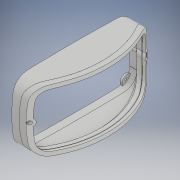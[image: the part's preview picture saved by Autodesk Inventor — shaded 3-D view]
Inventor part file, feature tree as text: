
AUTODESK INVENTOR PART (.ipt)
format: ipt  version: 2019 (Build 230136000, 136)  size: 3,016,704 bytes
history: native  units: mm
features: extrude x15, sketch x11, projected_geometry x7, other x4, hole x3, plane x3, fillet x1
ambient origin geometry x8: Origin, YZ Plane, XZ Plane, XY Plane, X Axis, Y Axis, Z Axis, Center Point
bodies: Volumenkörper3 (feature_tree), Volumenkörper7 (feature_tree), Volumenkörper8 (feature_tree), Volumenkörper9 (feature_tree), Volumenkörper11 (feature_tree)
feature tree (44):
  sketch  "Skizze1"  dims[d8=1.000002mm d10=3.000002mm]
  extrude  "Extrusion3"  Depth=3.000002mm
  extrude  "Extrusion4"  Depth=10.0mm TaperAngle=0.0deg
  sketch  "Skizze2"  dims[d11=1.2mm d12=0.0mm d13=10.0mm d14=0.0mm]
  extrude  "Extrusion5"  Depth=8.0mm
  sketch  "Skizze3"  dims[d16=8.0mm d17=8.0mm]
  hole  "Bohrung1"  [1 undecoded]
  extrude  "Extrusion7"  Depth=138.0mm
  plane  "Arbeitsebene1"
  plane  "Arbeitsebene2"
  extrude  "Extrusion14"  Depth=10.0mm TaperAngle=0.0deg
  sketch  "Skizze7"  dims[d20=3.0mm d21=0.0mm]
  extrude  "Extrusion11"  Depth=140.0mm
  extrude  "Extrusion15"  Depth=3.0mm
  extrude  "Extrusion13"  Depth=6.0mm
  extrude  "Extrusion16"  Depth=3.000001mm
  extrude  "Extrusion17"  Depth=40.0mm TaperAngle=0.0deg
  extrude  "Extrusion20"  Depth=50.0mm TaperAngle=0.0deg
  extrude  "Extrusion21"  Depth=40.0mm TaperAngle=0.0deg
  other  "Kombinieren1"
  extrude  "Extrusion22"  Depth=0.499998mm
  other  "Kombinieren2"
  fillet  "Rundung1"  Radius=50.0mm
  plane  "Arbeitsebene4"
  sketch  "Skizze17"  dims[d49=3.0mm d50=3.0mm]
  hole  "Bohrung3"  [1 undecoded]
  hole  "Bohrung4"  [1 undecoded]
  extrude  "Extrusion25"  Depth=40.0mm TaperAngle=0.0deg
  other  "Kombinieren4"
  extrude  "Extrusion26"  Depth=0.75mm
  other  "Bild1"
  projected_geometry  "Projizierte Kontur1"
  sketch  "Skizze6"  dims[d18=8.0mm d19=8.0mm]
  projected_geometry  "Projizierte Kontur3"
  sketch  "Skizze9"  dims[d26=3.5mm d27=6.0mm d28=4.0mm d29=2.0mm d30=90.0deg d31=8.0mm d32=20.594885mm d33=138.0mm]
  projected_geometry  "Projizierte Kontur4"
  sketch  "Skizze10"  dims[d34=138.0mm d35=10.0mm d36=0.0mm]
  projected_geometry  "Projizierte Kontur5"
  sketch  "Skizze12"  dims[d43=40.0mm d44=0.0mm d45=140.0mm]
  projected_geometry  "Projizierte Kontur7"
  projected_geometry  "Projizierte Kontur10"
  sketch  "Skizze18"  dims[d51=40.0mm d52=0.0mm d53=6.0mm]
  sketch  "Skizze19"  dims[d54=40.0mm d55=0.0mm d56=3.000001mm d57=40.0mm d58=0.0mm d59=50.0mm d60=0.0mm d61=40.0mm d62=0.0mm d63=0.499998mm d69=50.0mm d70=0.0mm d71=40.0mm d72=0.0mm d73=5.0mm d74=40.0mm d75=0.0mm d76=0.75mm d77=3.0mm d95=50.0mm d96=6.0mm d97=6.0mm d98=3.0mm d99=6.0mm d100=4.0mm d101=2.0mm d102=90.0deg d103=8.0mm d104=20.594885mm d105=5.5mm d106=6.0mm d107=4.0mm d108=2.0mm d109=90.0deg d110=30.0mm d111=0.0mm d112=40.0mm d113=0.0mm d114=10.0mm d115=0.0mm]
  projected_geometry  "Projizierte Kontur11"
note: 3 required parameter values undecoded (feature->parameter linkage not recoverable at this tier; creation-order binding heuristic only, values carry confidence <= 0.55)
